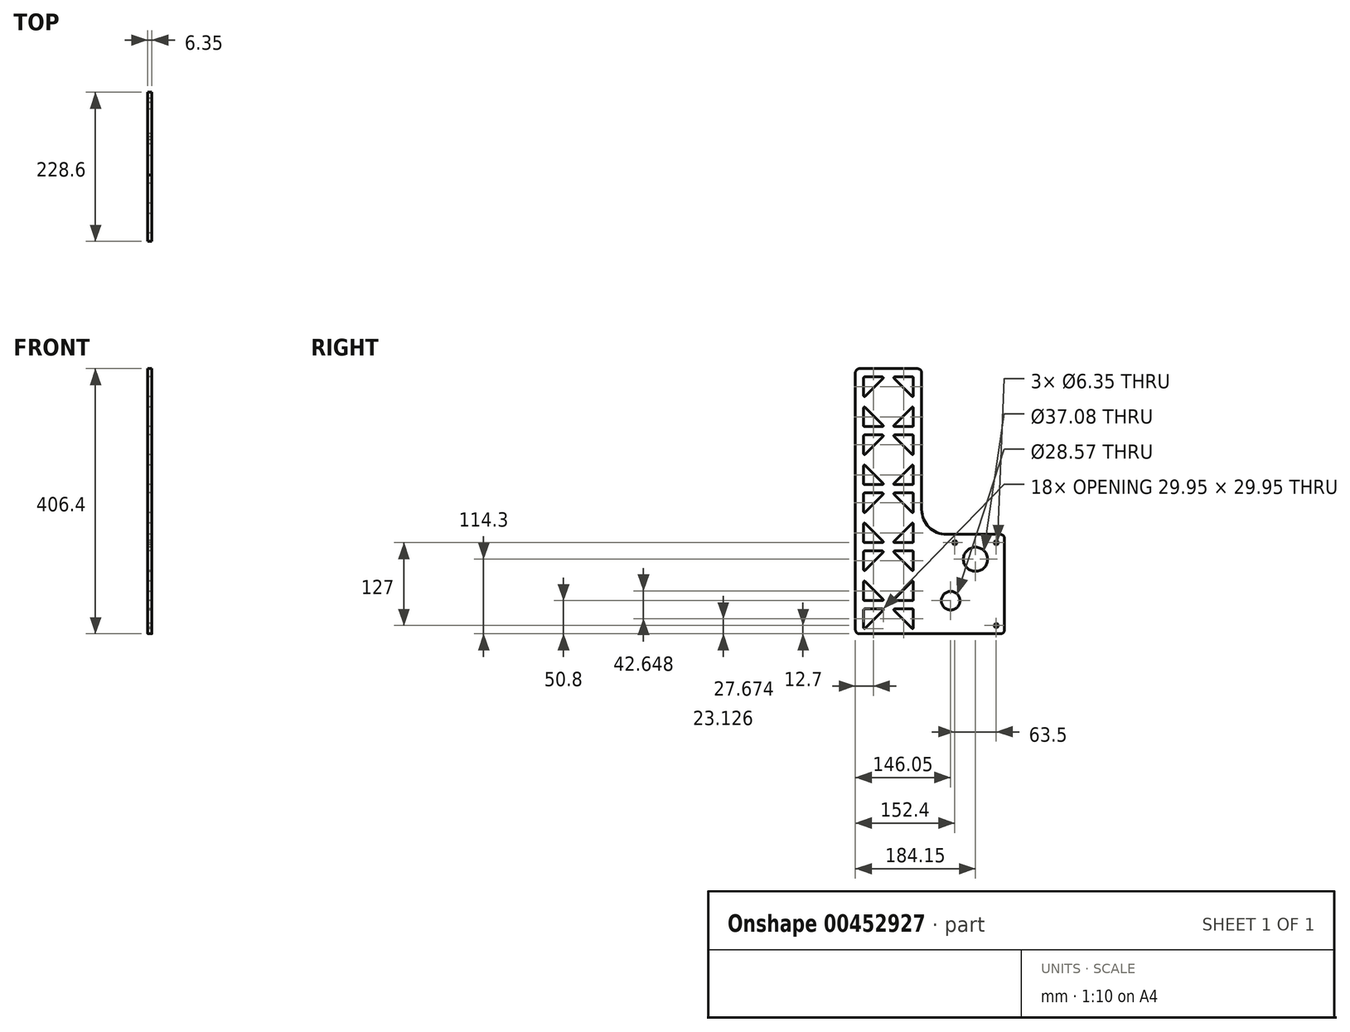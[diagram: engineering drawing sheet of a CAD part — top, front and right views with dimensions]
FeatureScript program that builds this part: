
annotation { "Feature Type Name" : "Feature", "Feature Type Description" : "" }
export const myFeature = defineFeature(function(context is Context, id is Id, definition is map)
    precondition{}
    {
        {
            var Q0;
            Q0=qCreatedBy(makeId("Right.planeOp"),FACE);
            var sketch = newSketch(context, id + "F0", { "sketchPlane" : qUnion([Q0])});
            skLineSegment(sketch, "E0.bottom", {"start": v(0, 0) * mm, "end": v(101.6, 0) * mm});
            skLineSegment(sketch, "E0.top", {"start": v(0, 406.4) * mm, "end": v(101.6, 406.4) * mm});
            skLineSegment(sketch, "E0.left", {"start": v(0, 0) * mm, "end": v(0, 406.4) * mm});
            skLineSegment(sketch, "E0.right", {"start": v(101.6, 0) * mm, "end": v(101.6, 406.4) * mm});
            skLineSegment(sketch, "E1.bottom", {"start": v(101.6, 0) * mm, "end": v(228.6, 0) * mm});
            skLineSegment(sketch, "E1.top", {"start": v(101.6, 152.4) * mm, "end": v(228.6, 152.4) * mm});
            skLineSegment(sketch, "E1.left", {"start": v(101.6, 0) * mm, "end": v(101.6, 152.4) * mm});
            skLineSegment(sketch, "E1.right", {"start": v(228.6, 0) * mm, "end": v(228.6, 152.4) * mm});
            skCircle(sketch, "E2", {"center": v(146.05, 50.8) * mm, "radius": 14.29 * mm});
            skCircle(sketch, "E3", {"center": v(146.05, 50.8) * mm, "radius": 50.8 * mm, "construction": true});
            skCircle(sketch, "E4", {"center": v(184.15, 114.3) * mm, "radius": 18.54 * mm});
            skCircle(sketch, "E5", {"center": v(215.9, 12.7) * mm, "radius": 3.18 * mm});
            skCircle(sketch, "E6", {"center": v(215.9, 139.7) * mm, "radius": 3.18 * mm});
            skLineSegment(sketch, "E7", {"start": v(87.63, 393.7) * mm, "end": v(60.22, 393.7) * mm});
            skLineSegment(sketch, "E8", {"start": v(59.32, 391.53) * mm, "end": v(86.73, 364.12) * mm});
            skLineSegment(sketch, "E9", {"start": v(88.9, 365.02) * mm, "end": v(88.9, 392.43) * mm});
            skPoint(sketch, "E10.visualSharp", {"position": v(57.15, 393.7) * mm});
            skArc(sketch, "E10.filletArc", {"start": v(60.22, 393.7) * mm, "mid": v(59.04, 392.92) * mm, "end": v(59.32, 391.53) * mm});
            skPoint(sketch, "E11.visualSharp", {"position": v(88.9, 361.95) * mm});
            skArc(sketch, "E12.filletArc", {"start": v(86.73, 364.12) * mm, "mid": v(88.12, 363.84) * mm, "end": v(88.9, 365.02) * mm});
            skPoint(sketch, "E13.visualSharp", {"position": v(88.9, 393.7) * mm});
            skArc(sketch, "E13.filletArc", {"start": v(88.9, 392.43) * mm, "mid": v(88.53, 393.33) * mm, "end": v(87.63, 393.7) * mm});
            skPoint(sketch, "E14.startSnap0", {"position": v(50.8, 406.4) * mm});
            skLineSegment(sketch, "E15", {"start": v(50.8, 406.4) * mm, "end": v(50.8, -18.77) * mm, "construction": true});
            skPoint(sketch, "E15.endSnap0", {"position": v(50.8, 0) * mm});
            skArc(sketch, "E16.MirrorCS", {"start": v(12.7, 392.43) * mm, "mid": v(13.07, 393.33) * mm, "end": v(13.97, 393.7) * mm});
            skArc(sketch, "E17.MirrorCS", {"start": v(41.38, 393.7) * mm, "mid": v(42.56, 392.92) * mm, "end": v(42.28, 391.53) * mm});
            skPoint(sketch, "E18.MirrorP", {"position": v(12.7, 361.95) * mm});
            skLineSegment(sketch, "E19.MirrorCS", {"start": v(13.97, 393.7) * mm, "end": v(41.38, 393.7) * mm});
            skPoint(sketch, "E20.MirrorP", {"position": v(12.7, 393.7) * mm});
            skLineSegment(sketch, "E21.MirrorCS", {"start": v(42.28, 391.53) * mm, "end": v(14.87, 364.12) * mm});
            skPoint(sketch, "E22.MirrorP", {"position": v(44.45, 393.7) * mm});
            skArc(sketch, "E23.MirrorCS", {"start": v(14.87, 364.12) * mm, "mid": v(13.48, 363.84) * mm, "end": v(12.7, 365.02) * mm});
            skLineSegment(sketch, "E24.MirrorCS", {"start": v(12.7, 365.02) * mm, "end": v(12.7, 392.43) * mm});
            skLineSegment(sketch, "E25", {"start": v(-14.42, 355.6) * mm, "end": v(137.53, 355.6) * mm, "construction": true});
            skArc(sketch, "E26.MirrorCS", {"start": v(12.7, 318.77) * mm, "mid": v(13.07, 317.87) * mm, "end": v(13.97, 317.5) * mm});
            skArc(sketch, "E27.MirrorCS", {"start": v(60.22, 317.5) * mm, "mid": v(59.04, 318.28) * mm, "end": v(59.32, 319.67) * mm});
            skArc(sketch, "E28.MirrorCS", {"start": v(14.87, 347.08) * mm, "mid": v(13.48, 347.36) * mm, "end": v(12.7, 346.18) * mm});
            skArc(sketch, "E29.MirrorCS", {"start": v(41.38, 317.5) * mm, "mid": v(42.56, 318.28) * mm, "end": v(42.28, 319.67) * mm});
            skArc(sketch, "E30.MirrorCS", {"start": v(86.73, 347.08) * mm, "mid": v(88.12, 347.36) * mm, "end": v(88.9, 346.18) * mm});
            skArc(sketch, "E31.MirrorCS", {"start": v(88.9, 318.77) * mm, "mid": v(88.53, 317.87) * mm, "end": v(87.63, 317.5) * mm});
            skPoint(sketch, "E32.MirrorP", {"position": v(12.7, 349.25) * mm});
            skPoint(sketch, "E33.MirrorP", {"position": v(88.9, 349.25) * mm});
            skPoint(sketch, "E34.MirrorP", {"position": v(12.7, 317.5) * mm});
            skPoint(sketch, "E35.MirrorP", {"position": v(44.45, 317.5) * mm});
            skLineSegment(sketch, "E36.MirrorCS", {"start": v(50.8, 304.8) * mm, "end": v(50.8, 729.97) * mm, "construction": true});
            skPoint(sketch, "E37.MirrorP", {"position": v(88.9, 317.5) * mm});
            skLineSegment(sketch, "E38.MirrorCS", {"start": v(12.7, 346.18) * mm, "end": v(12.7, 318.77) * mm});
            skLineSegment(sketch, "E39.MirrorCS", {"start": v(88.9, 346.18) * mm, "end": v(88.9, 318.77) * mm});
            skLineSegment(sketch, "E40.MirrorCS", {"start": v(42.28, 319.67) * mm, "end": v(14.87, 347.08) * mm});
            skLineSegment(sketch, "E41.MirrorCS", {"start": v(13.97, 317.5) * mm, "end": v(41.38, 317.5) * mm});
            skPoint(sketch, "E42.MirrorP", {"position": v(57.15, 317.5) * mm});
            skLineSegment(sketch, "E43.MirrorCS", {"start": v(87.63, 317.5) * mm, "end": v(60.22, 317.5) * mm});
            skLineSegment(sketch, "E44.MirrorCS", {"start": v(59.32, 319.67) * mm, "end": v(86.73, 347.08) * mm});
            skPoint(sketch, "E45.0.1.0", {"position": v(44.45, 304.8) * mm});
            skLineSegment(sketch, "E45.0.1.1", {"start": v(12.7, 276.12) * mm, "end": v(12.7, 303.53) * mm});
            skPoint(sketch, "E45.0.1.2", {"position": v(12.7, 273.05) * mm});
            skPoint(sketch, "E45.0.1.3", {"position": v(12.7, 304.8) * mm});
            skLineSegment(sketch, "E45.0.1.4", {"start": v(42.28, 302.63) * mm, "end": v(14.87, 275.22) * mm});
            skLineSegment(sketch, "E45.0.1.5", {"start": v(13.97, 304.8) * mm, "end": v(41.38, 304.8) * mm});
            skPoint(sketch, "E45.0.1.6", {"position": v(12.7, 273.05) * mm});
            skArc(sketch, "E45.0.1.7", {"start": v(14.87, 275.22) * mm, "mid": v(13.48, 274.94) * mm, "end": v(12.7, 276.12) * mm});
            skArc(sketch, "E45.0.1.8", {"start": v(41.38, 304.8) * mm, "mid": v(42.56, 304.02) * mm, "end": v(42.28, 302.63) * mm});
            skArc(sketch, "E45.0.1.9", {"start": v(12.7, 303.53) * mm, "mid": v(13.07, 304.43) * mm, "end": v(13.97, 304.8) * mm});
            skPoint(sketch, "E45.0.1.10", {"position": v(44.45, 228.6) * mm});
            skLineSegment(sketch, "E45.0.1.11", {"start": v(13.97, 228.6) * mm, "end": v(41.38, 228.6) * mm});
            skPoint(sketch, "E45.0.1.12", {"position": v(12.7, 260.35) * mm});
            skLineSegment(sketch, "E45.0.1.13", {"start": v(42.28, 230.77) * mm, "end": v(14.87, 258.18) * mm});
            skPoint(sketch, "E45.0.1.14", {"position": v(12.7, 228.6) * mm});
            skLineSegment(sketch, "E45.0.1.15", {"start": v(12.7, 257.28) * mm, "end": v(12.7, 229.87) * mm});
            skPoint(sketch, "E45.0.1.16", {"position": v(12.7, 260.35) * mm});
            skArc(sketch, "E45.0.1.17", {"start": v(41.38, 228.6) * mm, "mid": v(42.56, 229.38) * mm, "end": v(42.28, 230.77) * mm});
            skArc(sketch, "E45.0.1.18", {"start": v(14.87, 258.18) * mm, "mid": v(13.48, 258.46) * mm, "end": v(12.7, 257.28) * mm});
            skArc(sketch, "E45.0.1.19", {"start": v(12.7, 229.87) * mm, "mid": v(13.07, 228.97) * mm, "end": v(13.97, 228.6) * mm});
            skPoint(sketch, "E45.0.1.20", {"position": v(57.15, 228.6) * mm});
            skPoint(sketch, "E45.0.1.21", {"position": v(88.9, 228.6) * mm});
            skLineSegment(sketch, "E45.0.1.22", {"start": v(59.32, 230.77) * mm, "end": v(86.73, 258.18) * mm});
            skLineSegment(sketch, "E45.0.1.23", {"start": v(87.63, 228.6) * mm, "end": v(60.22, 228.6) * mm});
            skPoint(sketch, "E45.0.1.24", {"position": v(88.9, 260.35) * mm});
            skLineSegment(sketch, "E45.0.1.25", {"start": v(88.9, 257.28) * mm, "end": v(88.9, 229.87) * mm});
            skPoint(sketch, "E45.0.1.26", {"position": v(88.9, 260.35) * mm});
            skArc(sketch, "E45.0.1.27", {"start": v(60.22, 228.6) * mm, "mid": v(59.04, 229.38) * mm, "end": v(59.32, 230.77) * mm});
            skArc(sketch, "E45.0.1.28", {"start": v(88.9, 229.87) * mm, "mid": v(88.53, 228.97) * mm, "end": v(87.63, 228.6) * mm});
            skArc(sketch, "E45.0.1.29", {"start": v(86.73, 258.18) * mm, "mid": v(88.12, 258.46) * mm, "end": v(88.9, 257.28) * mm});
            skLineSegment(sketch, "E45.0.1.30", {"start": v(88.9, 276.12) * mm, "end": v(88.9, 303.53) * mm});
            skLineSegment(sketch, "E45.0.1.31", {"start": v(59.32, 302.63) * mm, "end": v(86.73, 275.22) * mm});
            skLineSegment(sketch, "E45.0.1.32", {"start": v(87.63, 304.8) * mm, "end": v(60.22, 304.8) * mm});
            skPoint(sketch, "E45.0.1.33", {"position": v(88.9, 304.8) * mm});
            skPoint(sketch, "E45.0.1.34", {"position": v(88.9, 273.05) * mm});
            skPoint(sketch, "E45.0.1.35", {"position": v(57.15, 304.8) * mm});
            skPoint(sketch, "E45.0.1.36", {"position": v(88.9, 273.05) * mm});
            skArc(sketch, "E45.0.1.37", {"start": v(86.73, 275.22) * mm, "mid": v(88.12, 274.94) * mm, "end": v(88.9, 276.12) * mm});
            skArc(sketch, "E45.0.1.38", {"start": v(88.9, 303.53) * mm, "mid": v(88.53, 304.43) * mm, "end": v(87.63, 304.8) * mm});
            skArc(sketch, "E45.0.1.39", {"start": v(60.22, 304.8) * mm, "mid": v(59.04, 304.02) * mm, "end": v(59.32, 302.63) * mm});
            skPoint(sketch, "E45.0.2.0", {"position": v(44.45, 215.9) * mm});
            skLineSegment(sketch, "E45.0.2.1", {"start": v(12.7, 187.22) * mm, "end": v(12.7, 214.63) * mm});
            skPoint(sketch, "E45.0.2.2", {"position": v(12.7, 184.15) * mm});
            skPoint(sketch, "E45.0.2.3", {"position": v(12.7, 215.9) * mm});
            skLineSegment(sketch, "E45.0.2.4", {"start": v(42.28, 213.73) * mm, "end": v(14.87, 186.32) * mm});
            skLineSegment(sketch, "E45.0.2.5", {"start": v(13.97, 215.9) * mm, "end": v(41.38, 215.9) * mm});
            skPoint(sketch, "E45.0.2.6", {"position": v(12.7, 184.15) * mm});
            skArc(sketch, "E45.0.2.7", {"start": v(14.87, 186.32) * mm, "mid": v(13.48, 186.04) * mm, "end": v(12.7, 187.22) * mm});
            skArc(sketch, "E45.0.2.8", {"start": v(41.38, 215.9) * mm, "mid": v(42.56, 215.12) * mm, "end": v(42.28, 213.73) * mm});
            skArc(sketch, "E45.0.2.9", {"start": v(12.7, 214.63) * mm, "mid": v(13.07, 215.53) * mm, "end": v(13.97, 215.9) * mm});
            skPoint(sketch, "E45.0.2.10", {"position": v(44.45, 139.7) * mm});
            skLineSegment(sketch, "E45.0.2.11", {"start": v(13.97, 139.7) * mm, "end": v(41.38, 139.7) * mm});
            skPoint(sketch, "E45.0.2.12", {"position": v(12.7, 171.45) * mm});
            skLineSegment(sketch, "E45.0.2.13", {"start": v(42.28, 141.87) * mm, "end": v(14.87, 169.28) * mm});
            skPoint(sketch, "E45.0.2.14", {"position": v(12.7, 139.7) * mm});
            skLineSegment(sketch, "E45.0.2.15", {"start": v(12.7, 168.38) * mm, "end": v(12.7, 140.97) * mm});
            skPoint(sketch, "E45.0.2.16", {"position": v(12.7, 171.45) * mm});
            skArc(sketch, "E45.0.2.17", {"start": v(41.38, 139.7) * mm, "mid": v(42.56, 140.48) * mm, "end": v(42.28, 141.87) * mm});
            skArc(sketch, "E45.0.2.18", {"start": v(14.87, 169.28) * mm, "mid": v(13.48, 169.56) * mm, "end": v(12.7, 168.38) * mm});
            skArc(sketch, "E45.0.2.19", {"start": v(12.7, 140.97) * mm, "mid": v(13.07, 140.07) * mm, "end": v(13.97, 139.7) * mm});
            skPoint(sketch, "E45.0.2.20", {"position": v(57.15, 139.7) * mm});
            skPoint(sketch, "E45.0.2.21", {"position": v(88.9, 139.7) * mm});
            skLineSegment(sketch, "E45.0.2.22", {"start": v(59.32, 141.87) * mm, "end": v(86.73, 169.28) * mm});
            skLineSegment(sketch, "E45.0.2.23", {"start": v(87.63, 139.7) * mm, "end": v(60.22, 139.7) * mm});
            skPoint(sketch, "E45.0.2.24", {"position": v(88.9, 171.45) * mm});
            skLineSegment(sketch, "E45.0.2.25", {"start": v(88.9, 168.38) * mm, "end": v(88.9, 140.97) * mm});
            skPoint(sketch, "E45.0.2.26", {"position": v(88.9, 171.45) * mm});
            skArc(sketch, "E45.0.2.27", {"start": v(60.22, 139.7) * mm, "mid": v(59.04, 140.48) * mm, "end": v(59.32, 141.87) * mm});
            skArc(sketch, "E45.0.2.28", {"start": v(88.9, 140.97) * mm, "mid": v(88.53, 140.07) * mm, "end": v(87.63, 139.7) * mm});
            skArc(sketch, "E45.0.2.29", {"start": v(86.73, 169.28) * mm, "mid": v(88.12, 169.56) * mm, "end": v(88.9, 168.38) * mm});
            skLineSegment(sketch, "E45.0.2.30", {"start": v(88.9, 187.22) * mm, "end": v(88.9, 214.63) * mm});
            skLineSegment(sketch, "E45.0.2.31", {"start": v(59.32, 213.73) * mm, "end": v(86.73, 186.32) * mm});
            skLineSegment(sketch, "E45.0.2.32", {"start": v(87.63, 215.9) * mm, "end": v(60.22, 215.9) * mm});
            skPoint(sketch, "E45.0.2.33", {"position": v(88.9, 215.9) * mm});
            skPoint(sketch, "E45.0.2.34", {"position": v(88.9, 184.15) * mm});
            skPoint(sketch, "E45.0.2.35", {"position": v(57.15, 215.9) * mm});
            skPoint(sketch, "E45.0.2.36", {"position": v(88.9, 184.15) * mm});
            skArc(sketch, "E45.0.2.37", {"start": v(86.73, 186.32) * mm, "mid": v(88.12, 186.04) * mm, "end": v(88.9, 187.22) * mm});
            skArc(sketch, "E45.0.2.38", {"start": v(88.9, 214.63) * mm, "mid": v(88.53, 215.53) * mm, "end": v(87.63, 215.9) * mm});
            skArc(sketch, "E45.0.2.39", {"start": v(60.22, 215.9) * mm, "mid": v(59.04, 215.12) * mm, "end": v(59.32, 213.73) * mm});
            skLineSegment(sketch, "E45.direction1", {"start": v(12.7, 317.5) * mm, "end": v(12.65, 317.5) * mm, "construction": true});
            skLineSegment(sketch, "E45.direction2", {"start": v(12.7, 317.5) * mm, "end": v(12.7, 228.6) * mm, "construction": true});
            skPoint(sketch, "E46.0.0.3", {"position": v(44.45, 127) * mm});
            skLineSegment(sketch, "E46.1.0.3", {"start": v(12.7, 98.32) * mm, "end": v(12.7, 125.73) * mm});
            skPoint(sketch, "E46.4.0.3", {"position": v(12.7, 95.25) * mm});
            skPoint(sketch, "E46.5.0.3", {"position": v(12.7, 127) * mm});
            skLineSegment(sketch, "E46.6.0.3", {"start": v(42.28, 124.83) * mm, "end": v(14.87, 97.42) * mm});
            skLineSegment(sketch, "E46.9.0.3", {"start": v(13.97, 127) * mm, "end": v(41.38, 127) * mm});
            skPoint(sketch, "E46.12.0.3", {"position": v(12.7, 95.25) * mm});
            skArc(sketch, "E46.13.0.3", {"start": v(14.87, 97.42) * mm, "mid": v(13.48, 97.14) * mm, "end": v(12.7, 98.32) * mm});
            skArc(sketch, "E46.17.0.3", {"start": v(41.38, 127) * mm, "mid": v(42.56, 126.22) * mm, "end": v(42.28, 124.83) * mm});
            skArc(sketch, "E46.21.0.3", {"start": v(12.7, 125.73) * mm, "mid": v(13.07, 126.63) * mm, "end": v(13.97, 127) * mm});
            skPoint(sketch, "E46.25.0.3", {"position": v(44.45, 50.8) * mm});
            skLineSegment(sketch, "E46.26.0.3", {"start": v(13.97, 50.8) * mm, "end": v(41.38, 50.8) * mm});
            skPoint(sketch, "E46.29.0.3", {"position": v(12.7, 82.55) * mm});
            skLineSegment(sketch, "E46.30.0.3", {"start": v(42.28, 52.97) * mm, "end": v(14.87, 80.38) * mm});
            skPoint(sketch, "E46.33.0.3", {"position": v(12.7, 50.8) * mm});
            skLineSegment(sketch, "E46.34.0.3", {"start": v(12.7, 79.48) * mm, "end": v(12.7, 52.07) * mm});
            skPoint(sketch, "E46.37.0.3", {"position": v(12.7, 82.55) * mm});
            skArc(sketch, "E46.38.0.3", {"start": v(41.38, 50.8) * mm, "mid": v(42.56, 51.58) * mm, "end": v(42.28, 52.97) * mm});
            skArc(sketch, "E46.42.0.3", {"start": v(14.87, 80.38) * mm, "mid": v(13.48, 80.66) * mm, "end": v(12.7, 79.48) * mm});
            skArc(sketch, "E46.46.0.3", {"start": v(12.7, 52.07) * mm, "mid": v(13.07, 51.17) * mm, "end": v(13.97, 50.8) * mm});
            skPoint(sketch, "E46.50.0.3", {"position": v(57.15, 50.8) * mm});
            skPoint(sketch, "E46.51.0.3", {"position": v(88.9, 50.8) * mm});
            skLineSegment(sketch, "E46.52.0.3", {"start": v(59.32, 52.97) * mm, "end": v(86.73, 80.38) * mm});
            skLineSegment(sketch, "E46.55.0.3", {"start": v(87.63, 50.8) * mm, "end": v(60.22, 50.8) * mm});
            skPoint(sketch, "E46.58.0.3", {"position": v(88.9, 82.55) * mm});
            skLineSegment(sketch, "E46.59.0.3", {"start": v(88.9, 79.48) * mm, "end": v(88.9, 52.07) * mm});
            skPoint(sketch, "E46.62.0.3", {"position": v(88.9, 82.55) * mm});
            skArc(sketch, "E46.63.0.3", {"start": v(60.22, 50.8) * mm, "mid": v(59.04, 51.58) * mm, "end": v(59.32, 52.97) * mm});
            skArc(sketch, "E46.67.0.3", {"start": v(88.9, 52.07) * mm, "mid": v(88.53, 51.17) * mm, "end": v(87.63, 50.8) * mm});
            skArc(sketch, "E46.71.0.3", {"start": v(86.73, 80.38) * mm, "mid": v(88.12, 80.66) * mm, "end": v(88.9, 79.48) * mm});
            skLineSegment(sketch, "E46.75.0.3", {"start": v(88.9, 98.32) * mm, "end": v(88.9, 125.73) * mm});
            skLineSegment(sketch, "E46.78.0.3", {"start": v(59.32, 124.83) * mm, "end": v(86.73, 97.42) * mm});
            skLineSegment(sketch, "E46.81.0.3", {"start": v(87.63, 127) * mm, "end": v(60.22, 127) * mm});
            skPoint(sketch, "E46.84.0.3", {"position": v(88.9, 127) * mm});
            skPoint(sketch, "E46.85.0.3", {"position": v(88.9, 95.25) * mm});
            skPoint(sketch, "E46.86.0.3", {"position": v(57.15, 127) * mm});
            skPoint(sketch, "E46.87.0.3", {"position": v(88.9, 95.25) * mm});
            skArc(sketch, "E46.88.0.3", {"start": v(86.73, 97.42) * mm, "mid": v(88.12, 97.14) * mm, "end": v(88.9, 98.32) * mm});
            skArc(sketch, "E46.92.0.3", {"start": v(88.9, 125.73) * mm, "mid": v(88.53, 126.63) * mm, "end": v(87.63, 127) * mm});
            skArc(sketch, "E46.96.0.3", {"start": v(60.22, 127) * mm, "mid": v(59.04, 126.22) * mm, "end": v(59.32, 124.83) * mm});
            skPoint(sketch, "E46.0.0.4", {"position": v(44.45, 38.1) * mm});
            skLineSegment(sketch, "E46.1.0.4", {"start": v(12.7, 9.42) * mm, "end": v(12.7, 36.83) * mm});
            skPoint(sketch, "E46.4.0.4", {"position": v(12.7, 6.35) * mm});
            skPoint(sketch, "E46.5.0.4", {"position": v(12.7, 38.1) * mm});
            skLineSegment(sketch, "E46.6.0.4", {"start": v(42.28, 35.93) * mm, "end": v(14.87, 8.52) * mm});
            skLineSegment(sketch, "E46.9.0.4", {"start": v(13.97, 38.1) * mm, "end": v(41.38, 38.1) * mm});
            skPoint(sketch, "E46.12.0.4", {"position": v(12.7, 6.35) * mm});
            skArc(sketch, "E46.13.0.4", {"start": v(14.87, 8.52) * mm, "mid": v(13.48, 8.24) * mm, "end": v(12.7, 9.42) * mm});
            skArc(sketch, "E46.17.0.4", {"start": v(41.38, 38.1) * mm, "mid": v(42.56, 37.32) * mm, "end": v(42.28, 35.93) * mm});
            skArc(sketch, "E46.21.0.4", {"start": v(12.7, 36.83) * mm, "mid": v(13.07, 37.73) * mm, "end": v(13.97, 38.1) * mm});
            skLineSegment(sketch, "E46.75.0.4", {"start": v(88.9, 9.42) * mm, "end": v(88.9, 36.83) * mm});
            skLineSegment(sketch, "E46.78.0.4", {"start": v(59.32, 35.93) * mm, "end": v(86.73, 8.52) * mm});
            skLineSegment(sketch, "E46.81.0.4", {"start": v(87.63, 38.1) * mm, "end": v(60.22, 38.1) * mm});
            skPoint(sketch, "E46.84.0.4", {"position": v(88.9, 38.1) * mm});
            skPoint(sketch, "E46.85.0.4", {"position": v(88.9, 6.35) * mm});
            skPoint(sketch, "E46.86.0.4", {"position": v(57.15, 38.1) * mm});
            skPoint(sketch, "E46.87.0.4", {"position": v(88.9, 6.35) * mm});
            skArc(sketch, "E46.88.0.4", {"start": v(86.73, 8.52) * mm, "mid": v(88.12, 8.24) * mm, "end": v(88.9, 9.42) * mm});
            skArc(sketch, "E46.92.0.4", {"start": v(88.9, 36.83) * mm, "mid": v(88.53, 37.73) * mm, "end": v(87.63, 38.1) * mm});
            skArc(sketch, "E46.96.0.4", {"start": v(60.22, 38.1) * mm, "mid": v(59.04, 37.32) * mm, "end": v(59.32, 35.93) * mm});
            skArc(sketch, "E47", {"start": v(101.6, 190.5) * mm, "mid": v(112.76, 163.56) * mm, "end": v(139.7, 152.4) * mm});
            skLineSegment(sketch, "E48", {"start": v(139.7, 190.5) * mm, "end": v(101.6, 190.5) * mm});
            skCircle(sketch, "E49", {"center": v(215.9, 139.7) * mm, "radius": 6.35 * mm, "construction": true});
            skCircle(sketch, "E50", {"center": v(152.4, 139.7) * mm, "radius": 3.18 * mm});
            skCircle(sketch, "E51", {"center": v(152.4, 139.7) * mm, "radius": 6.35 * mm, "construction": true});
            skCircle(sketch, "E52", {"center": v(215.9, 12.7) * mm, "radius": 6.35 * mm, "construction": true});
            skSolve(sketch);
        }
        {
            var Q0;
            Q0=makeQuery(id+"F0.imprint","IMPRINT",FACE,{"disambiguationData":[TD([[makeQuery(id+"F0.imprint","IMPRINT",EDGE,{"derivedFrom":sQuery(id+"F0.wireOp",EDGE,"E0.bottom")}),1.0]])]});
            var Q1;
            Q1=makeQuery(id+"F0.imprint","IMPRINT",FACE,{"disambiguationData":[TD([[makeQuery(id+"F0.imprint","IMPRINT",EDGE,{"derivedFrom":sQuery(id+"F0.wireOp",EDGE,"E1.bottom")}),1.0]])]});
            var Q2;
            {var subQ3=sQuery(id+"F0.wireOp",EDGE,"E47");Q2=makeQuery(id+"F0.imprint","IMPRINT",FACE,{"disambiguationData":[TD([[makeQuery(id+"F0.imprint","IMPRINT",EDGE,{"derivedFrom":subQ3}),-1.0]])]});}
            extrude(context, id + "F1", {"entities" : qUnion([Q0, Q1, Q2]), "depth" : 6.35 * mm});
        }
        {
            var Q0;
            Q0=makeQuery(id+"F1.opExtrude","SWEPT_EDGE",EDGE,{"disambiguationData":[OSD([sQuery(id+"F0.wireOp",EDGE,"E1.bottom"),sQuery(id+"F0.wireOp",EDGE,"E1.right")])]});
            var Q1;
            Q1=makeQuery(id+"F1.opExtrude","SWEPT_EDGE",EDGE,{"disambiguationData":[OSD([sQuery(id+"F0.wireOp",EDGE,"E1.top"),sQuery(id+"F0.wireOp",EDGE,"E1.right")])]});
            var Q2;
            Q2=makeQuery(id+"F1.opExtrude","SWEPT_EDGE",EDGE,{"disambiguationData":[OSD([sQuery(id+"F0.wireOp",EDGE,"E0.bottom"),sQuery(id+"F0.wireOp",EDGE,"E0.left")])]});
            var Q3;
            Q3=makeQuery(id+"F1.opExtrude","SWEPT_EDGE",EDGE,{"disambiguationData":[OSD([sQuery(id+"F0.wireOp",EDGE,"E0.top"),sQuery(id+"F0.wireOp",EDGE,"E0.left")])]});
            var Q4;
            Q4=makeQuery(id+"F1.opExtrude","SWEPT_EDGE",EDGE,{"disambiguationData":[OSD([sQuery(id+"F0.wireOp",EDGE,"E0.top"),sQuery(id+"F0.wireOp",EDGE,"E0.right")])]});
            fillet(context, id + "F2", {"entities" : qUnion([Q0, Q1, Q2, Q3, Q4]), "radius" : 6.35 * mm, "tangentPropagation" : true, "allowEdgeOverflow" : false});
        }
    });
